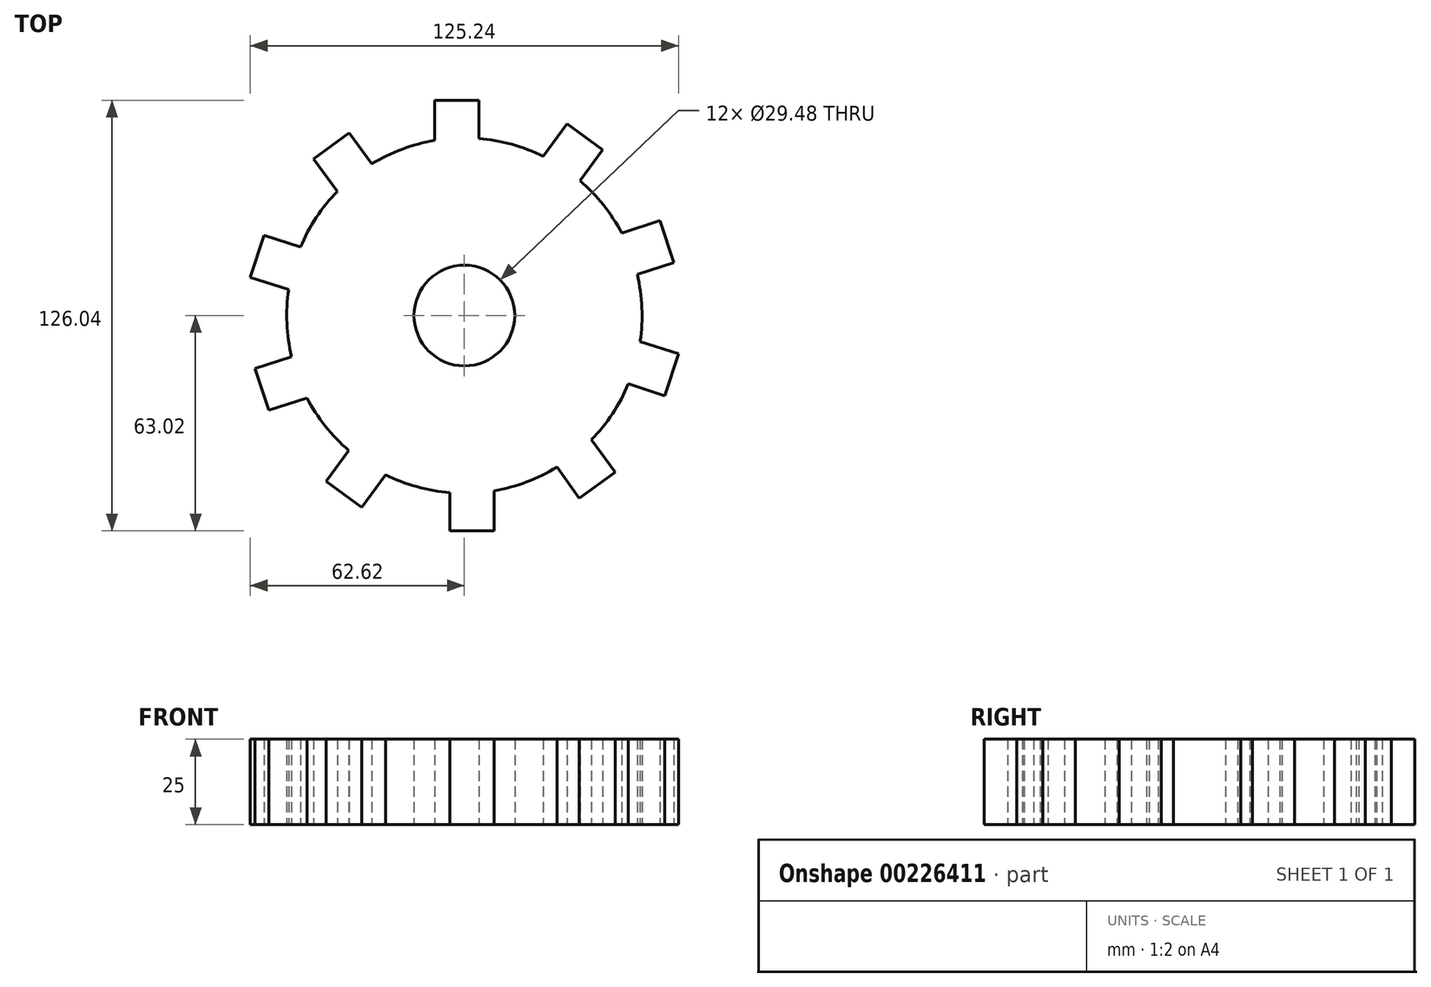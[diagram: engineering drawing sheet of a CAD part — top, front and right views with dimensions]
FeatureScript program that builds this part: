
annotation { "Feature Type Name" : "Feature", "Feature Type Description" : "" }
export const myFeature = defineFeature(function(context is Context, id is Id, definition is map)
    precondition{}
    {
        {
            var Q0;
            Q0=qCreatedBy(makeId("Top.planeOp"),FACE);
            var sketch = newSketch(context, id + "F0", { "sketchPlane" : qUnion([Q0])});
            skArc(sketch, "E0", {"start": v(-37.16, 36.35) * mm, "mid": v(-43.35, 28.7) * mm, "end": v(-47.98, 20) * mm});
            skLineSegment(sketch, "E1", {"start": v(-8.7, 51.25) * mm, "end": v(-8.7, 63.02) * mm});
            skLineSegment(sketch, "E2", {"start": v(4.2, 63.02) * mm, "end": v(4.2, 51.82) * mm});
            skLineSegment(sketch, "E3", {"start": v(-8.7, 63.02) * mm, "end": v(4.2, 63.02) * mm});
            skLineSegment(sketch, "E4.1.0", {"start": v(-37.16, 36.35) * mm, "end": v(-44.08, 45.87) * mm});
            skLineSegment(sketch, "E4.1.1", {"start": v(-44.08, 45.87) * mm, "end": v(-33.65, 53.45) * mm});
            skLineSegment(sketch, "E4.1.2", {"start": v(-33.65, 53.45) * mm, "end": v(-27.07, 44.38) * mm});
            skLineSegment(sketch, "E4.2.0", {"start": v(-51.43, 7.57) * mm, "end": v(-62.62, 11.2) * mm});
            skLineSegment(sketch, "E4.2.1", {"start": v(-62.62, 11.2) * mm, "end": v(-58.64, 23.46) * mm});
            skLineSegment(sketch, "E4.2.2", {"start": v(-58.64, 23.46) * mm, "end": v(-47.98, 20) * mm});
            skLineSegment(sketch, "E5.1.3.0", {"start": v(-46.06, -24.1) * mm, "end": v(-57.25, -27.75) * mm});
            skLineSegment(sketch, "E5.3.3.0", {"start": v(-57.25, -27.75) * mm, "end": v(-61.23, -15.49) * mm});
            skLineSegment(sketch, "E5.6.3.0", {"start": v(-61.23, -15.49) * mm, "end": v(-50.58, -12.03) * mm});
            skLineSegment(sketch, "E5.1.4.0", {"start": v(-23.09, -46.58) * mm, "end": v(-30, -56.1) * mm});
            skLineSegment(sketch, "E5.3.4.0", {"start": v(-30, -56.1) * mm, "end": v(-40.43, -48.52) * mm});
            skLineSegment(sketch, "E5.6.4.0", {"start": v(-40.43, -48.52) * mm, "end": v(-33.85, -39.46) * mm});
            skLineSegment(sketch, "E5.1.5.0", {"start": v(8.7, -51.25) * mm, "end": v(8.7, -63.02) * mm});
            skLineSegment(sketch, "E5.3.5.0", {"start": v(8.7, -63.02) * mm, "end": v(-4.2, -63.02) * mm});
            skLineSegment(sketch, "E5.6.5.0", {"start": v(-4.2, -63.02) * mm, "end": v(-4.2, -51.82) * mm});
            skLineSegment(sketch, "E5.1.6.0", {"start": v(37.16, -36.35) * mm, "end": v(44.08, -45.87) * mm});
            skLineSegment(sketch, "E5.3.6.0", {"start": v(44.08, -45.87) * mm, "end": v(33.65, -53.45) * mm});
            skLineSegment(sketch, "E5.6.6.0", {"start": v(33.65, -53.45) * mm, "end": v(27.07, -44.38) * mm});
            skLineSegment(sketch, "E5.1.7.0", {"start": v(51.43, -7.57) * mm, "end": v(62.62, -11.2) * mm});
            skLineSegment(sketch, "E5.3.7.0", {"start": v(62.62, -11.2) * mm, "end": v(58.64, -23.46) * mm});
            skLineSegment(sketch, "E5.6.7.0", {"start": v(58.64, -23.46) * mm, "end": v(47.98, -20) * mm});
            skLineSegment(sketch, "E5.1.8.0", {"start": v(46.06, 24.1) * mm, "end": v(57.25, 27.75) * mm});
            skLineSegment(sketch, "E5.3.8.0", {"start": v(57.25, 27.75) * mm, "end": v(61.23, 15.49) * mm});
            skLineSegment(sketch, "E5.6.8.0", {"start": v(61.23, 15.49) * mm, "end": v(50.58, 12.03) * mm});
            skLineSegment(sketch, "E5.1.9.0", {"start": v(23.09, 46.58) * mm, "end": v(30, 56.1) * mm});
            skLineSegment(sketch, "E5.3.9.0", {"start": v(30, 56.1) * mm, "end": v(40.43, 48.52) * mm});
            skLineSegment(sketch, "E5.6.9.0", {"start": v(40.43, 48.52) * mm, "end": v(33.85, 39.46) * mm});
            skArc(sketch, "E6.trimOffspring", {"start": v(-8.7, 51.25) * mm, "mid": v(-18.2, 48.7) * mm, "end": v(-27.07, 44.38) * mm});
            skArc(sketch, "E7.trimOffspring", {"start": v(23.09, 46.58) * mm, "mid": v(13.9, 50.1) * mm, "end": v(4.2, 51.82) * mm});
            skArc(sketch, "E8.trimOffspring", {"start": v(46.06, 24.1) * mm, "mid": v(40.68, 32.36) * mm, "end": v(33.85, 39.46) * mm});
            skArc(sketch, "E9.trimOffspring", {"start": v(51.43, -7.57) * mm, "mid": v(51.94, 2.27) * mm, "end": v(50.58, 12.03) * mm});
            skArc(sketch, "E10.trimOffspring", {"start": v(37.16, -36.35) * mm, "mid": v(43.35, -28.7) * mm, "end": v(47.98, -20) * mm});
            skArc(sketch, "E11.trimOffspring", {"start": v(8.7, -51.25) * mm, "mid": v(18.2, -48.7) * mm, "end": v(27.07, -44.38) * mm});
            skArc(sketch, "E12.trimOffspring", {"start": v(-23.09, -46.58) * mm, "mid": v(-13.9, -50.1) * mm, "end": v(-4.2, -51.82) * mm});
            skArc(sketch, "E13.trimOffspring", {"start": v(-46.06, -24.1) * mm, "mid": v(-40.68, -32.36) * mm, "end": v(-33.85, -39.46) * mm});
            skArc(sketch, "E14.trimOffspring", {"start": v(-51.43, 7.57) * mm, "mid": v(-51.94, -2.27) * mm, "end": v(-50.58, -12.03) * mm});
            skCircle(sketch, "E15", {"center": v(0, 0) * mm, "radius": 14.74 * mm});
            skSolve(sketch);
        }
        {
            var Q0;
            Q0=makeQuery(id+"F0.imprint","IMPRINT",FACE,{"disambiguationData":[TD([[makeQuery(id+"F0.imprint","IMPRINT",EDGE,{"derivedFrom":sQuery(id+"F0.wireOp",EDGE,"E0")}),1.0]])]});
            extrude(context, id + "F1", {"entities" : qUnion([Q0]), "depth" : 25 * mm});
        }
    });
